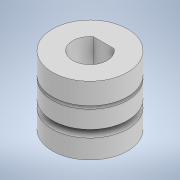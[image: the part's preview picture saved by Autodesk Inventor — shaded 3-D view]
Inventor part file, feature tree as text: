
AUTODESK INVENTOR PART (.ipt)
format: ipt  version: 2022.2 (Build 262287000, 287)  size: 145,920 bytes
history: native  units: mm
features: sketch x2, other x1, extrude x1, revolve x1
ambient origin geometry x8: Origin, YZ Plane, XZ Plane, XY Plane, X Axis, Y Axis, Z Axis, Center Point
bodies: Solid1 (feature_tree)
feature tree (5):
  other  "Motor.ipt"
  extrude  "Extrusion1"  Depth=10.0mm
  revolve  "Revolution1"  [1 undecoded]
  sketch  "Sketch1"  dims[d0=10.0mm d1=11.0mm]
  sketch  "Sketch2"  dims[d2=5.05mm d3=2.02mm d4=10.0mm d5=0.0mm d8=0.4mm d9=1.0mm d10=0.44mm d11=1.1mm d12=30.0deg d13=30.0deg d14=90.0deg]
note: 1 required parameter value undecoded (feature->parameter linkage not recoverable at this tier; creation-order binding heuristic only, values carry confidence <= 0.55)
